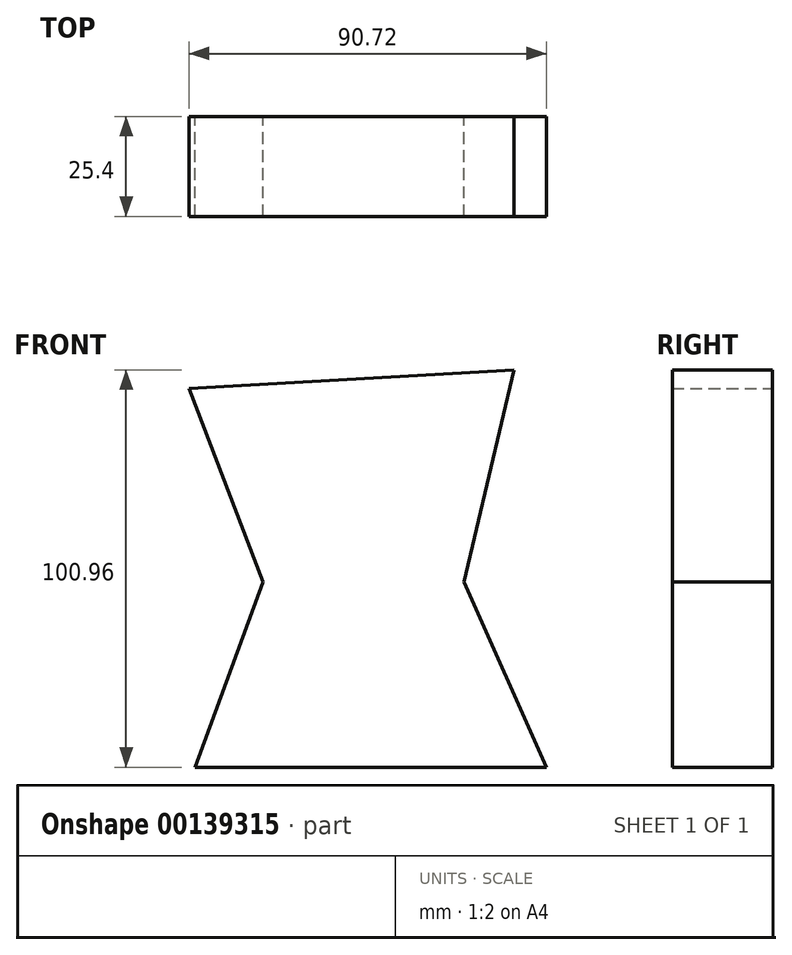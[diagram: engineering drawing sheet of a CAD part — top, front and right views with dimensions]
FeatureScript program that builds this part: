
annotation { "Feature Type Name" : "Feature", "Feature Type Description" : "" }
export const myFeature = defineFeature(function(context is Context, id is Id, definition is map)
    precondition{}
    {
        {
            var Q0;
            Q0=qCreatedBy(makeId("Front.planeOp"),FACE);
            var sketch = newSketch(context, id + "F0", { "sketchPlane" : qUnion([Q0])});
            skLineSegment(sketch, "E0", {"start": v(-45.36, 49.12) * mm, "end": v(-26.55, 0) * mm});
            skLineSegment(sketch, "E1", {"start": v(-26.55, 0) * mm, "end": v(-43.9, -47.03) * mm});
            skLineSegment(sketch, "E2", {"start": v(-43.9, -47.03) * mm, "end": v(45.36, -47.03) * mm});
            skLineSegment(sketch, "E3", {"start": v(45.36, -47.03) * mm, "end": v(24.46, 0) * mm});
            skLineSegment(sketch, "E4", {"start": v(24.46, 0) * mm, "end": v(37.2, 53.93) * mm});
            skLineSegment(sketch, "E5", {"start": v(37.2, 53.93) * mm, "end": v(-45.36, 49.12) * mm});
            skSolve(sketch);
        }
        {
            var Q0;
            Q0 = qSketchRegion(id + "F0", true);
            var Q1;
            Q1=makeQuery(id+"F0.imprint","IMPRINT",FACE,{"disambiguationData":[TD([[makeQuery(id+"F0.imprint","IMPRINT",EDGE,{"derivedFrom":sQuery(id+"F0.wireOp",EDGE,"E0")}),1.0]])]});
            extrude(context, id + "F1", {"entities" : qUnion([Q0, Q1]), "depth" : 25.4 * mm});
        }
    });
